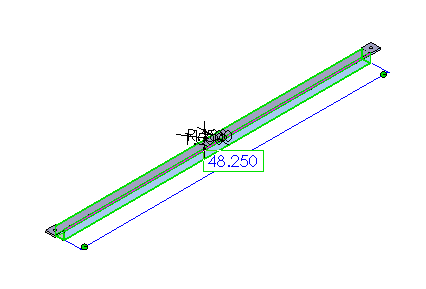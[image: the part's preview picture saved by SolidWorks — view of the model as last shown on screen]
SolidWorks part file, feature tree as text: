
SOLIDWORKS PART (.sldprt)
format: sldprt  version: not decoded by parser v0  size: 208,384 bytes
history: native  units: mm
features: sketch x4, extrude x3, shell x1, cut_extrude x1 (+11 scaffold rows collapsed)
feature tree (20):
  scaffold x11  (default folders/planes/origin — collapsed)
  sketch  "Sketch1"  dims[D3=4.7625mm D1=38.1mm D2=38.1mm]
  extrude  "Extrude1"  Depth=1225.55mm
  shell  "Shell1"  Thickness=2.54mm
  sketch  "Sketch2"  dims[D1=6.35mm]
  extrude  "Extrude2"  Depth=38.1mm
  sketch  "Sketch3"
  extrude  "Extrude3"  Depth=38.1mm
  sketch  "Sketch4"  dims[D1=9.525mm D2=9.525mm]
  cut_extrude  "Cut-Extrude1"  [1 undecoded]
decode coverage: 7 of 9 modeling features carry decoded parameters
note: 1 parameter value undecoded
note: suppression state not decoded; provenance and decode notes live in map.json
